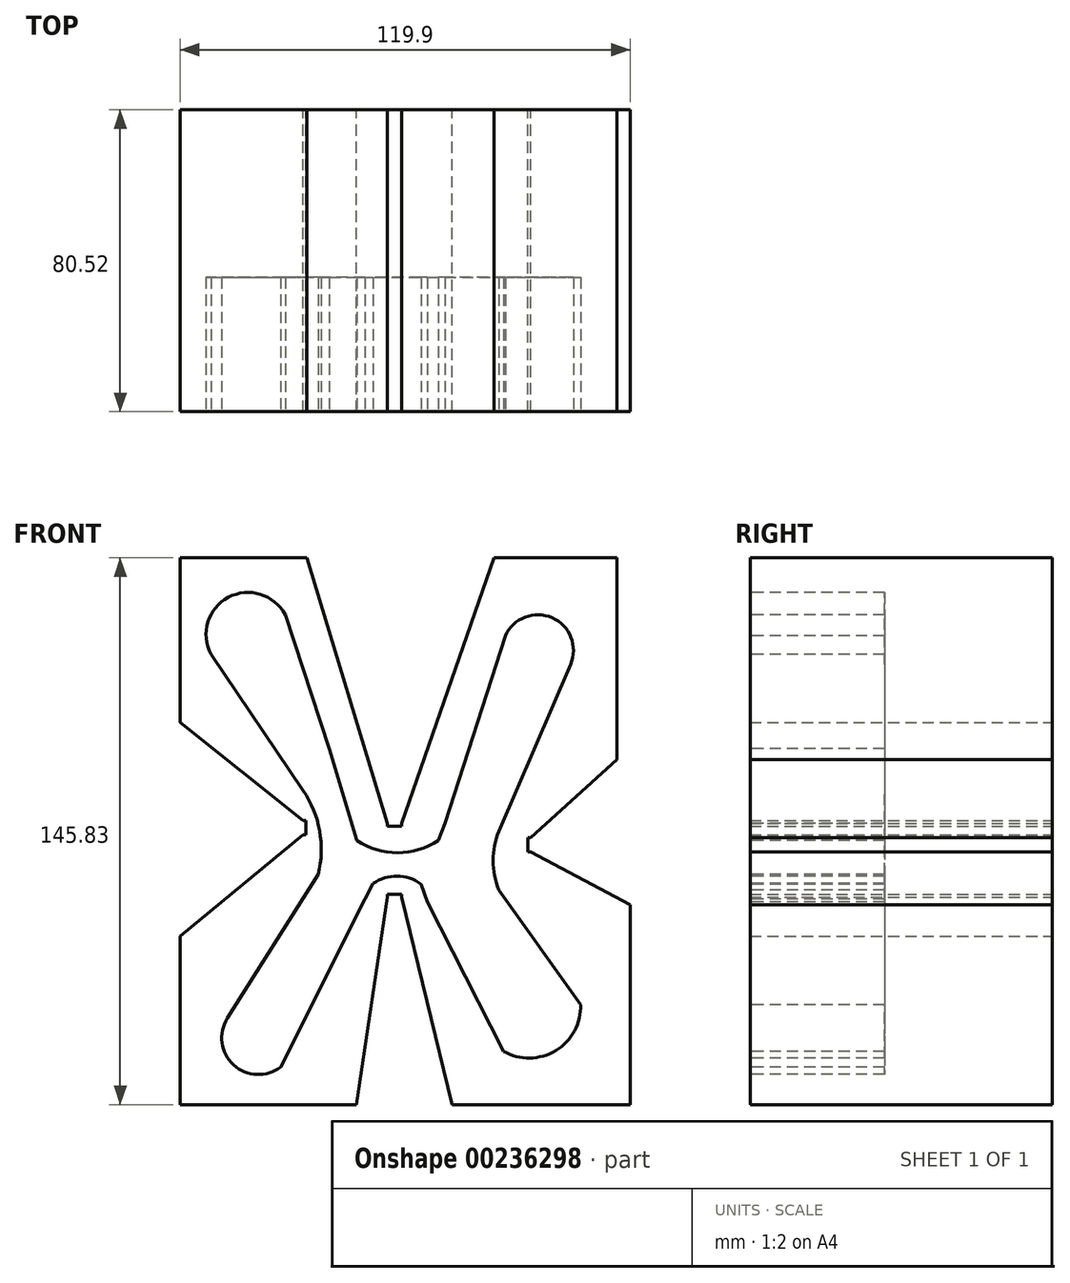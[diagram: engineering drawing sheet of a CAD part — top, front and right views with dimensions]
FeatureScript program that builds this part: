
annotation { "Feature Type Name" : "Feature", "Feature Type Description" : "" }
export const myFeature = defineFeature(function(context is Context, id is Id, definition is map)
    precondition{}
    {
        {
            var Q0;
            Q0=qCreatedBy(makeId("Front.planeOp"),FACE);
            var sketch = newSketch(context, id + "F0", { "sketchPlane" : qUnion([Q0])});
            skLineSegment(sketch, "E0", {"start": v(0, 0) * mm, "end": v(-21.36, 70.76) * mm});
            skLineSegment(sketch, "E1", {"start": v(-21.36, 70.76) * mm, "end": v(-55.14, 70.76) * mm});
            skLineSegment(sketch, "E2", {"start": v(-55.14, 70.76) * mm, "end": v(-55.14, 26.82) * mm});
            skLineSegment(sketch, "E3", {"start": v(-55.14, 26.82) * mm, "end": v(-22.4, 0.66) * mm});
            skLineSegment(sketch, "E4", {"start": v(-22.4, 0.66) * mm, "end": v(-21.63, 0.66) * mm});
            skLineSegment(sketch, "E5", {"start": v(-21.63, 0.66) * mm, "end": v(-21.63, -3.15) * mm});
            skLineSegment(sketch, "E6", {"start": v(-21.63, -3.15) * mm, "end": v(-22.4, -3.15) * mm});
            skLineSegment(sketch, "E7", {"start": v(-22.4, -3.15) * mm, "end": v(-55.14, -30.11) * mm});
            skLineSegment(sketch, "E8", {"start": v(-55.14, -30.11) * mm, "end": v(-55.14, -75.07) * mm});
            skLineSegment(sketch, "E9", {"start": v(-55.14, -75.07) * mm, "end": v(-8.15, -75.07) * mm});
            skLineSegment(sketch, "E10", {"start": v(3.8, 0) * mm, "end": v(28.46, 70.76) * mm});
            skLineSegment(sketch, "E11", {"start": v(28.46, 70.76) * mm, "end": v(61.22, 70.76) * mm});
            skLineSegment(sketch, "E12", {"start": v(61.22, 70.76) * mm, "end": v(61.22, 16.91) * mm});
            skLineSegment(sketch, "E13", {"start": v(61.22, 16.91) * mm, "end": v(38.27, -3.9) * mm});
            skLineSegment(sketch, "E14", {"start": v(38.27, -3.9) * mm, "end": v(37.5, -3.9) * mm});
            skLineSegment(sketch, "E15", {"start": v(37.5, -3.9) * mm, "end": v(37.5, -7.72) * mm});
            skLineSegment(sketch, "E16", {"start": v(37.5, -7.72) * mm, "end": v(38.27, -7.72) * mm});
            skLineSegment(sketch, "E17", {"start": v(38.27, -7.72) * mm, "end": v(64.76, -21.73) * mm});
            skLineSegment(sketch, "E18", {"start": v(64.76, -21.73) * mm, "end": v(64.76, -75.07) * mm});
            skLineSegment(sketch, "E19", {"start": v(64.76, -75.07) * mm, "end": v(17.26, -75.07) * mm});
            skLineSegment(sketch, "E20", {"start": v(17.26, -75.07) * mm, "end": v(3.8, -19.79) * mm});
            skLineSegment(sketch, "E21", {"start": v(-8.15, -75.07) * mm, "end": v(0, -19.79) * mm});
            skLineSegment(sketch, "E22", {"start": v(0, -19.79) * mm, "end": v(0, -19.03) * mm});
            skLineSegment(sketch, "E23", {"start": v(3.8, -19.79) * mm, "end": v(3.8, -19.03) * mm});
            skLineSegment(sketch, "E24", {"start": v(3.81, -19.03) * mm, "end": v(0, -19.03) * mm});
            skLineSegment(sketch, "E25", {"start": v(0, 0) * mm, "end": v(0, -0.76) * mm});
            skLineSegment(sketch, "E26", {"start": v(3.8, 0) * mm, "end": v(3.8, -0.76) * mm});
            skLineSegment(sketch, "E27", {"start": v(0, -0.76) * mm, "end": v(3.8, -0.76) * mm});
            skSolve(sketch);
        }
        {
            var Q0;
            Q0 = qSketchRegion(id + "F0", true);
            extrude(context, id + "F1", {"entities" : qUnion([Q0]), "depth" : 80.52 * mm});
        }
        {
            var Q0;
            Q0=makeQuery(id+"F1.opExtrude","CAP_FACE",FACE,{"disambiguationData":[OSD([sQuery(id+"F0.wireOp",EDGE,"E0"),sQuery(id+"F0.wireOp",EDGE,"E1"),sQuery(id+"F0.wireOp",EDGE,"E2"),sQuery(id+"F0.wireOp",EDGE,"E3"),sQuery(id+"F0.wireOp",EDGE,"E4"),sQuery(id+"F0.wireOp",EDGE,"E5"),sQuery(id+"F0.wireOp",EDGE,"E6"),sQuery(id+"F0.wireOp",EDGE,"E7"),sQuery(id+"F0.wireOp",EDGE,"E8"),sQuery(id+"F0.wireOp",EDGE,"E9"),sQuery(id+"F0.wireOp",EDGE,"E10"),sQuery(id+"F0.wireOp",EDGE,"E11"),sQuery(id+"F0.wireOp",EDGE,"E12"),sQuery(id+"F0.wireOp",EDGE,"E13"),sQuery(id+"F0.wireOp",EDGE,"E14"),sQuery(id+"F0.wireOp",EDGE,"E15"),sQuery(id+"F0.wireOp",EDGE,"E16"),sQuery(id+"F0.wireOp",EDGE,"E17"),sQuery(id+"F0.wireOp",EDGE,"E18"),sQuery(id+"F0.wireOp",EDGE,"E19"),sQuery(id+"F0.wireOp",EDGE,"E20"),sQuery(id+"F0.wireOp",EDGE,"E21"),sQuery(id+"F0.wireOp",EDGE,"E22"),sQuery(id+"F0.wireOp",EDGE,"E23"),sQuery(id+"F0.wireOp",EDGE,"E24"),sQuery(id+"F0.wireOp",EDGE,"E25"),sQuery(id+"F0.wireOp",EDGE,"E26"),sQuery(id+"F0.wireOp",EDGE,"E27")])],"isStart":false});
            var sketch = newSketch(context, id + "F2", { "sketchPlane" : qUnion([Q0])});
            skLineSegment(sketch, "E28", {"start": v(-47, 45.06) * mm, "end": v(-22.4, 8.73) * mm});
            skLineSegment(sketch, "E29", {"start": v(-27.18, 55.58) * mm, "end": v(-15.44, 19.86) * mm});
            skArc(sketch, "E30", {"start": v(-27.18, 55.58) * mm, "mid": v(-42.35, 60.22) * mm, "end": v(-47, 45.06) * mm});
            skLineSegment(sketch, "E31", {"start": v(31.53, 49.95) * mm, "end": v(15.39, 0) * mm});
            skLineSegment(sketch, "E32", {"start": v(48.9, 42.36) * mm, "end": v(29.82, -2.16) * mm});
            skArc(sketch, "E33", {"start": v(48.9, 42.36) * mm, "mid": v(43.98, 54.78) * mm, "end": v(31.53, 49.95) * mm});
            skLineSegment(sketch, "E34", {"start": v(-18.37, -13.66) * mm, "end": v(-42.6, -52.07) * mm});
            skLineSegment(sketch, "E35", {"start": v(-5.9, -20.26) * mm, "end": v(-28.4, -65.03) * mm});
            skArc(sketch, "E36", {"start": v(-42.6, -52.07) * mm, "mid": v(-40.92, -64.48) * mm, "end": v(-28.4, -65.03) * mm});
            skLineSegment(sketch, "E37", {"start": v(10.74, -21) * mm, "end": v(31.04, -60.87) * mm});
            skLineSegment(sketch, "E38", {"start": v(29.82, -17.82) * mm, "end": v(51.6, -48.4) * mm});
            skArc(sketch, "E39", {"start": v(31.04, -60.87) * mm, "mid": v(44.98, -60.67) * mm, "end": v(51.6, -48.4) * mm});
            skLineSegment(sketch, "E40", {"start": v(-15.44, 19.86) * mm, "end": v(-8.04, -4.64) * mm});
            skLineSegment(sketch, "E41", {"start": v(15.39, 0) * mm, "end": v(13.6, -4.64) * mm});
            skLineSegment(sketch, "E42", {"start": v(-5.9, -20.26) * mm, "end": v(-3.71, -16.12) * mm});
            skLineSegment(sketch, "E43", {"start": v(10.74, -21) * mm, "end": v(9.02, -16.28) * mm});
            skArc(sketch, "E44", {"start": v(9.02, -16.28) * mm, "mid": v(2.68, -14.12) * mm, "end": v(-3.71, -16.12) * mm});
            skArc(sketch, "E45", {"start": v(-18.37, -13.66) * mm, "mid": v(-18.01, -2.04) * mm, "end": v(-22.4, 8.73) * mm});
            skArc(sketch, "E46", {"start": v(29.82, -2.16) * mm, "mid": v(28.21, -9.99) * mm, "end": v(29.82, -17.82) * mm});
            skArc(sketch, "E47", {"start": v(-8.04, -4.64) * mm, "mid": v(2.77, -7.91) * mm, "end": v(13.6, -4.64) * mm});
            skSolve(sketch);
        }
        {
            var Q0;
            Q0 = qSketchRegion(id + "F2", true);
            extrude(context, id + "F3", {"entities" : qUnion([Q0]), "operationType" : NewBodyOperationType.REMOVE, "oppositeDirection" : true, "depth" : 35.81 * mm});
        }
    });
